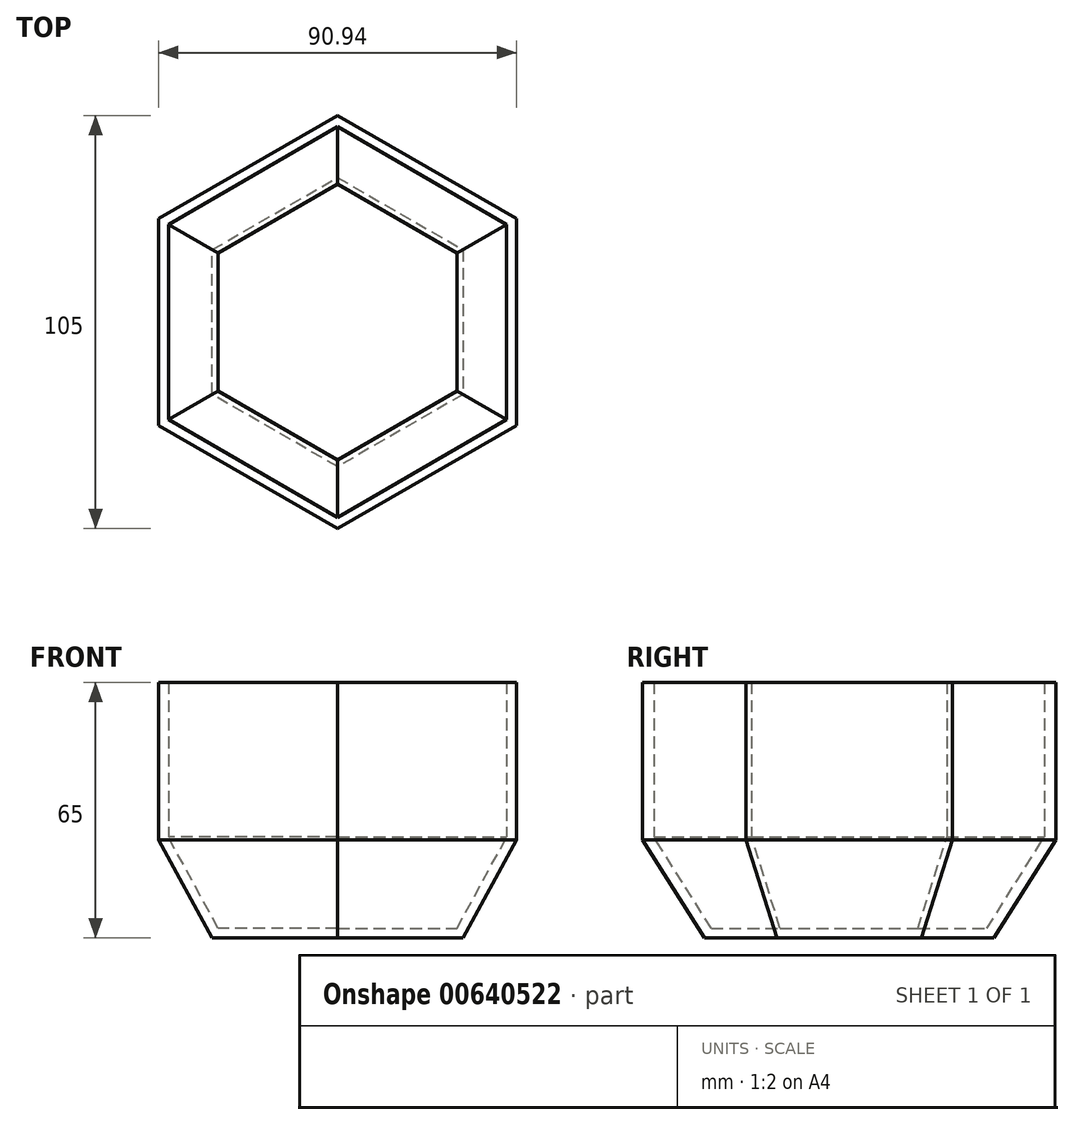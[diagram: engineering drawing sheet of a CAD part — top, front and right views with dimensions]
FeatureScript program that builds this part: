
annotation { "Feature Type Name" : "Feature", "Feature Type Description" : "" }
export const myFeature = defineFeature(function(context is Context, id is Id, definition is map)
    precondition{}
    {
        {
            assignVariable(context, id + "F0", {"name" : "h1", "anyValue" : 25});
        }
        {
            assignVariable(context, id + "F1", {"name" : "h2", "anyValue" : 40});
        }
        {
            var Q0;
            Q0=qCreatedBy(makeId("Top.planeOp"),FACE);
            var sketch = newSketch(context, id + "F2", { "sketchPlane" : qUnion([Q0])});
            skCircle(sketch, "E0.cCircle", {"center": v(0, 0) * mm, "radius": 36.75 * mm, "construction": true});
            skLineSegment(sketch, "E0.0", {"start": v(0, -36.75) * mm, "end": v(-31.83, -18.37) * mm});
            skLineSegment(sketch, "E0.1", {"start": v(-31.83, -18.37) * mm, "end": v(-31.83, 18.37) * mm});
            skLineSegment(sketch, "E0.2", {"start": v(-31.83, 18.37) * mm, "end": v(0, 36.75) * mm});
            skLineSegment(sketch, "E0.3", {"start": v(0, 36.75) * mm, "end": v(31.83, 18.38) * mm});
            skLineSegment(sketch, "E0.4", {"start": v(31.83, 18.38) * mm, "end": v(31.83, -18.38) * mm});
            skLineSegment(sketch, "E0.5", {"start": v(31.83, -18.38) * mm, "end": v(0, -36.75) * mm});
            skSolve(sketch);
        }
        {
            var Q0;
            Q0=makeQuery(id+"F2.imprint","IMPRINT",FACE,{"disambiguationData":[TD([[makeQuery(id+"F2.imprint","IMPRINT",EDGE,{"derivedFrom":sQuery(id+"F2.wireOp",EDGE,"E0.0")}),-1.0]])]});
            cPlane(context, id + "F3", {"entities" : qUnion([Q0]), "cplaneType" : CPlaneType.OFFSET, "offset" : (getVariable(context, 'h1')) * mm, "width" : 150 * mm, "height" : 150 * mm});
        }
        {
            var Q0;
            Q0=qCreatedBy(id+"F3.planeOp",FACE);
            var sketch = newSketch(context, id + "F4", { "sketchPlane" : qUnion([Q0])});
            skCircle(sketch, "E1.cCircle", {"center": v(0, 0) * mm, "radius": 52.5 * mm, "construction": true});
            skLineSegment(sketch, "E1.0", {"start": v(0, -52.5) * mm, "end": v(-45.47, -26.25) * mm});
            skLineSegment(sketch, "E1.1", {"start": v(-45.47, -26.25) * mm, "end": v(-45.47, 26.25) * mm});
            skLineSegment(sketch, "E1.2", {"start": v(-45.47, 26.25) * mm, "end": v(0, 52.5) * mm});
            skLineSegment(sketch, "E1.3", {"start": v(0, 52.5) * mm, "end": v(45.47, 26.25) * mm});
            skLineSegment(sketch, "E1.4", {"start": v(45.47, 26.25) * mm, "end": v(45.47, -26.25) * mm});
            skLineSegment(sketch, "E1.5", {"start": v(45.47, -26.25) * mm, "end": v(0, -52.5) * mm});
            skSolve(sketch);
        }
        {
            var Q0;
            Q0=makeQuery(id+"F2.imprint","IMPRINT",FACE,{"disambiguationData":[TD([[makeQuery(id+"F2.imprint","IMPRINT",EDGE,{"derivedFrom":sQuery(id+"F2.wireOp",EDGE,"E0.0")}),-1.0]])]});
            var Q1;
            Q1=makeQuery(id+"F4.imprint","IMPRINT",FACE,{"disambiguationData":[TD([[makeQuery(id+"F4.imprint","IMPRINT",EDGE,{"derivedFrom":sQuery(id+"F4.wireOp",EDGE,"E1.0")}),-1.0]])]});
            loft(context, id + "F5", {"sheetProfilesArray" : [{ "sheetProfileEntities" : qUnion([Q0]) }, { "sheetProfileEntities" : qUnion([Q1]) }]});
        }
        {
            var Q0;
            Q0=makeQuery(id+"F5.opLoft","CAP_FACE",FACE,{"disambiguationData":[OSD([makeQuery(id+"F4.imprint","IMPRINT",FACE,{"disambiguationData":[TD([[makeQuery(id+"F4.imprint","IMPRINT",EDGE,{"derivedFrom":sQuery(id+"F4.wireOp",EDGE,"E1.0")}),-1.0]])]})])],"isStart":true});
            extrude(context, id + "F6", {"entities" : qUnion([Q0]), "operationType" : NewBodyOperationType.ADD, "depth" : (getVariable(context, 'h2')) * mm, "offsetDistance" : 25 * mm});
        }
        {
            var Q0;
            Q0=makeQuery(id+"F6.opExtrude","CAP_FACE",FACE,{"disambiguationData":[OSD([makeQuery(id+"F4.imprint","IMPRINT",FACE,{"disambiguationData":[TD([[makeQuery(id+"F4.imprint","IMPRINT",EDGE,{"derivedFrom":sQuery(id+"F4.wireOp",EDGE,"E1.0")}),-1.0]])]})])],"isStart":false});
            shell(context, id + "F7", {"entities" : qUnion([Q0]), "thickness" : 2.5 * mm});
        }
    });
